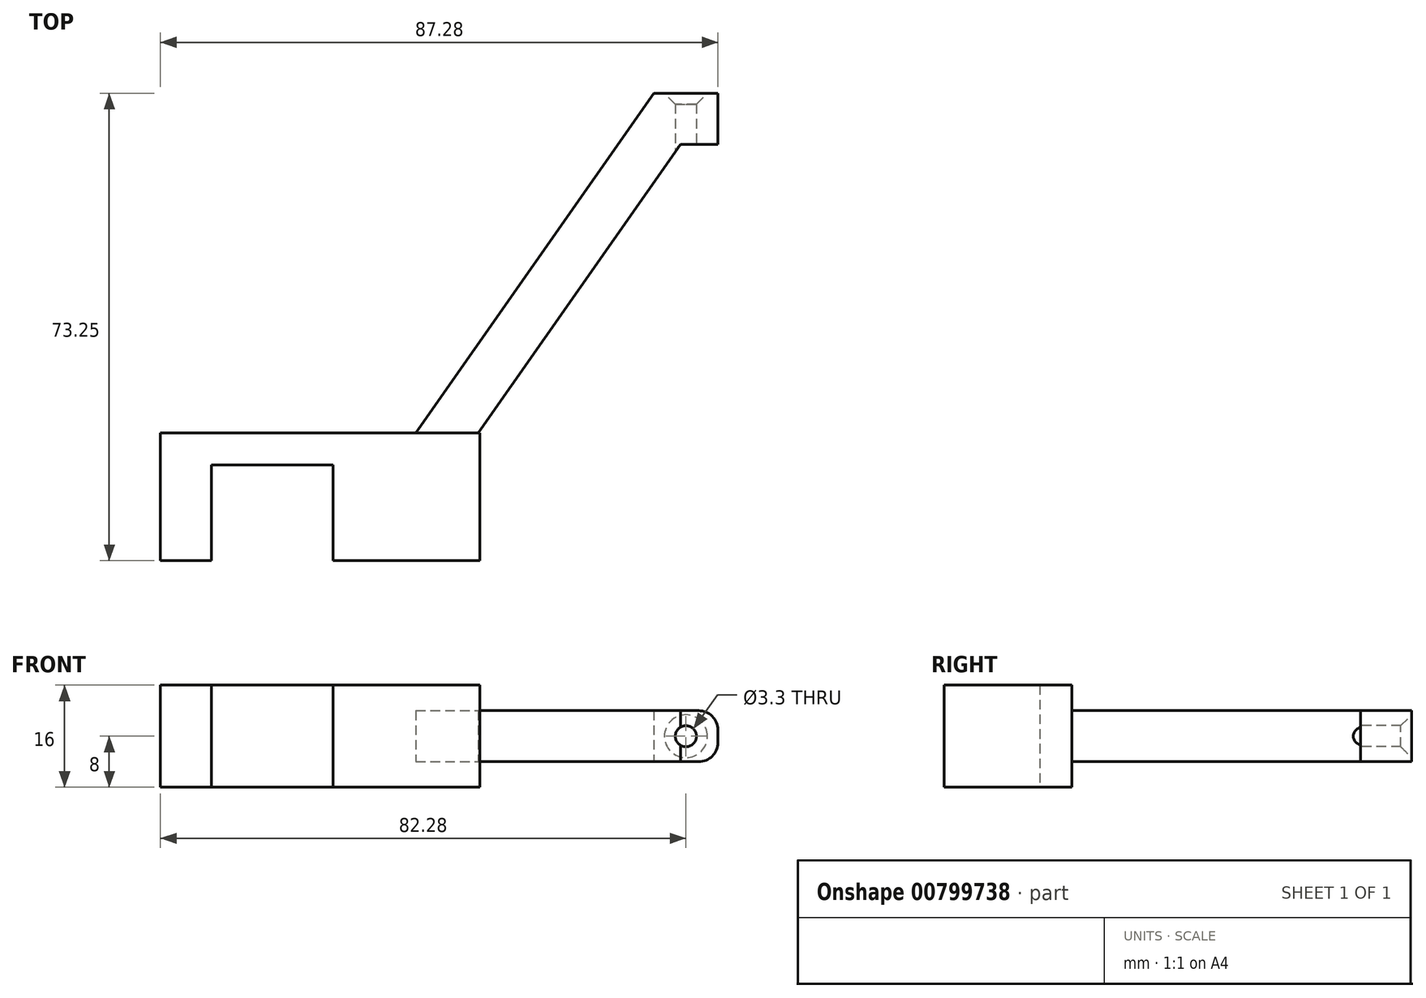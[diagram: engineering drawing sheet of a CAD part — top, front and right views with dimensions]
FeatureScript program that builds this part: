
annotation { "Feature Type Name" : "Feature", "Feature Type Description" : "" }
export const myFeature = defineFeature(function(context is Context, id is Id, definition is map)
    precondition{}
    {
        {
            var Q0;
            Q0=qCreatedBy(makeId("Top.planeOp"),FACE);
            var sketch = newSketch(context, id + "F0", { "sketchPlane" : qUnion([Q0])});
            skPoint(sketch, "E0.middle", {"position": v(0, 0) * mm});
            skLineSegment(sketch, "E1", {"start": v(6.97, 21.81) * mm, "end": v(44.25, 75.06) * mm});
            skLineSegment(sketch, "E2", {"start": v(44.25, 75.06) * mm, "end": v(54.25, 75.06) * mm});
            skLineSegment(sketch, "E3.0", {"start": v(48.41, 67.06) * mm, "end": v(54.25, 67.06) * mm});
            skLineSegment(sketch, "E3.1", {"start": v(13.52, 17.23) * mm, "end": v(48.41, 67.06) * mm});
            skLineSegment(sketch, "E4", {"start": v(54.25, 75.06) * mm, "end": v(54.25, 67.06) * mm});
            skLineSegment(sketch, "E5", {"start": v(6.97, 21.81) * mm, "end": v(6.97, 11.81) * mm});
            skLineSegment(sketch, "E6", {"start": v(6.97, 11.81) * mm, "end": v(16.97, 11.81) * mm});
            skLineSegment(sketch, "E7", {"start": v(16.97, 11.81) * mm, "end": v(16.97, 21.81) * mm});
            skLineSegment(sketch, "E8", {"start": v(6.97, 21.81) * mm, "end": v(16.97, 21.81) * mm});
            skPoint(sketch, "E9", {"position": v(-33.03, 21.81) * mm});
            skPoint(sketch, "E10", {"position": v(6.97, 1.81) * mm});
            skPoint(sketch, "E11", {"position": v(-33.03, 1.81) * mm});
            skPoint(sketch, "E12", {"position": v(16.97, 11.81) * mm});
            skPoint(sketch, "E13", {"position": v(16.97, 1.81) * mm});
            skLineSegment(sketch, "E14", {"start": v(-33.03, 21.81) * mm, "end": v(6.97, 21.81) * mm});
            skLineSegment(sketch, "E15", {"start": v(-33.03, 1.81) * mm, "end": v(16.97, 1.81) * mm});
            skLineSegment(sketch, "E16", {"start": v(16.97, 11.81) * mm, "end": v(16.97, 1.81) * mm});
            skLineSegment(sketch, "E17", {"start": v(-33.03, 21.81) * mm, "end": v(-33.03, 1.81) * mm});
            skPoint(sketch, "E18", {"position": v(-25.03, 1.81) * mm});
            skPoint(sketch, "E19", {"position": v(-6.03, 1.81) * mm});
            skPoint(sketch, "E20", {"position": v(-25.03, 16.81) * mm});
            skPoint(sketch, "E21", {"position": v(-6.03, 16.81) * mm});
            skLineSegment(sketch, "E22", {"start": v(-25.03, 1.81) * mm, "end": v(-25.03, 16.81) * mm});
            skLineSegment(sketch, "E23", {"start": v(-25.03, 16.81) * mm, "end": v(-6.03, 16.81) * mm});
            skLineSegment(sketch, "E24", {"start": v(-5.94, 15.98) * mm, "end": v(-6.03, 1.81) * mm});
            skLineSegment(sketch, "E25", {"start": v(-6.03, 16.81) * mm, "end": v(-6.03, 1.81) * mm});
            skSolve(sketch);
        }
        {
            var Q0;
            Q0=makeQuery(id+"F0.imprint","IMPRINT",FACE,{"disambiguationData":[TD([[makeQuery(id+"F0.imprint","IMPRINT",EDGE,{"derivedFrom":sQuery(id+"F0.wireOp",EDGE,"E1")}),-1.0]])]});
            extrude(context, id + "F1", {"entities" : qUnion([Q0]), "depth" : 8 * mm, "offsetDistance" : 25 * mm});
        }
        {
            var Q0;
            Q0=makeQuery(id+"F1.opExtrude","SWEPT_FACE",FACE,{"disambiguationData":[OSD([sQuery(id+"F0.wireOp",EDGE,"E2")])]});
            var sketch = newSketch(context, id + "F2", { "sketchPlane" : qUnion([Q0])});
            skPoint(sketch, "E26", {"position": v(-49.25, 4) * mm});
            skPoint(sketch, "E26.positionSnap0", {"position": v(-44.25, 4) * mm});
            skPoint(sketch, "E26.positionSnap1", {"position": v(-49.25, 0) * mm});
            skSolve(sketch);
        }
        {
            var Q0;
            Q0=sQuery(id+"F2.wireOp",VERTEX,"E26");
            var Q1;
            Q1=makeQuery(id+"F1.opExtrude","SWEPT_BODY",BODY,{"disambiguationData":[OSD([sQuery(id+"F0.wireOp",EDGE,"E1"),sQuery(id+"F0.wireOp",EDGE,"E2"),sQuery(id+"F0.wireOp",EDGE,"E3.0"),sQuery(id+"F0.wireOp",EDGE,"E3.1"),sQuery(id+"F0.wireOp",EDGE,"E4"),sQuery(id+"F0.wireOp",EDGE,"E7"),sQuery(id+"F0.wireOp",EDGE,"E8")])]});
            hole(context, id + "F3", {"style" : HoleStyle.C_SINK, "endStyle" : HoleEndStyle.THROUGH, "standardTappedOrClearance" : lookupTablePath({ "standard" : "ISO", "fit" : "Normal", "size" : "M3", "type" : "Clearance" }), "standardBlindInLast" : lookupTablePath({ "fit" : "Standard", "standard" : "ISO", "size" : "M3", "type" : "Clearance" }), "holeDiameter" : 3.3 * mm, "cSinkDiameter" : 6.72 * mm, "cSinkAngle" : 90 * degree, "majorDiameter" : 5 * mm, "isTappedThrough" : true, "tappedDepth" : 12 * mm, "tapClearance" : 3, "startFromSketch" : true, "locations" : qUnion([Q0]), "scope" : qUnion([Q1])});
        }
        {
            var Q0;
            Q0=makeQuery(id+"F0.imprint","IMPRINT",FACE,{"disambiguationData":[TD([[makeQuery(id+"F0.imprint","IMPRINT",EDGE,{"derivedFrom":sQuery(id+"F0.wireOp",EDGE,"E5")}),1.0]])]});
            var Q1;
            Q1=makeQuery(id+"F0.imprint","IMPRINT",FACE,{"disambiguationData":[TD([[makeQuery(id+"F0.imprint","IMPRINT",EDGE,{"derivedFrom":sQuery(id+"F0.wireOp",EDGE,"E5")}),-1.0]])]});
            extrude(context, id + "F4", {"entities" : qUnion([Q0, Q1]), "operationType" : NewBodyOperationType.ADD, "depth" : 12 * mm, "offsetDistance" : 25 * mm});
        }
        {
            var Q0;
            Q0=makeQuery(id+"F0.imprint","IMPRINT",FACE,{"disambiguationData":[TD([[makeQuery(id+"F0.imprint","IMPRINT",EDGE,{"derivedFrom":sQuery(id+"F0.wireOp",EDGE,"E5")}),-1.0]])]});
            var Q1;
            Q1=makeQuery(id+"F0.imprint","IMPRINT",FACE,{"disambiguationData":[TD([[makeQuery(id+"F0.imprint","IMPRINT",EDGE,{"derivedFrom":sQuery(id+"F0.wireOp",EDGE,"E5")}),1.0]])]});
            extrude(context, id + "F5", {"entities" : qUnion([Q0, Q1]), "operationType" : NewBodyOperationType.ADD, "oppositeDirection" : true, "depth" : 4 * mm, "offsetDistance" : 25 * mm});
        }
        {
            var Q0;
            Q0=makeQuery(id+"F1.opExtrude","CAP_EDGE",EDGE,{"disambiguationData":[OSD([sQuery(id+"F0.wireOp",EDGE,"E4")])],"isStart":true});
            var Q1;
            Q1=makeQuery(id+"F1.opExtrude","CAP_EDGE",EDGE,{"disambiguationData":[OSD([sQuery(id+"F0.wireOp",EDGE,"E4")])],"isStart":false});
            fillet(context, id + "F6", {"entities" : qUnion([Q0, Q1]), "radius" : 3 * mm, "tangentPropagation" : true, "allowEdgeOverflow" : false});
        }
    });
